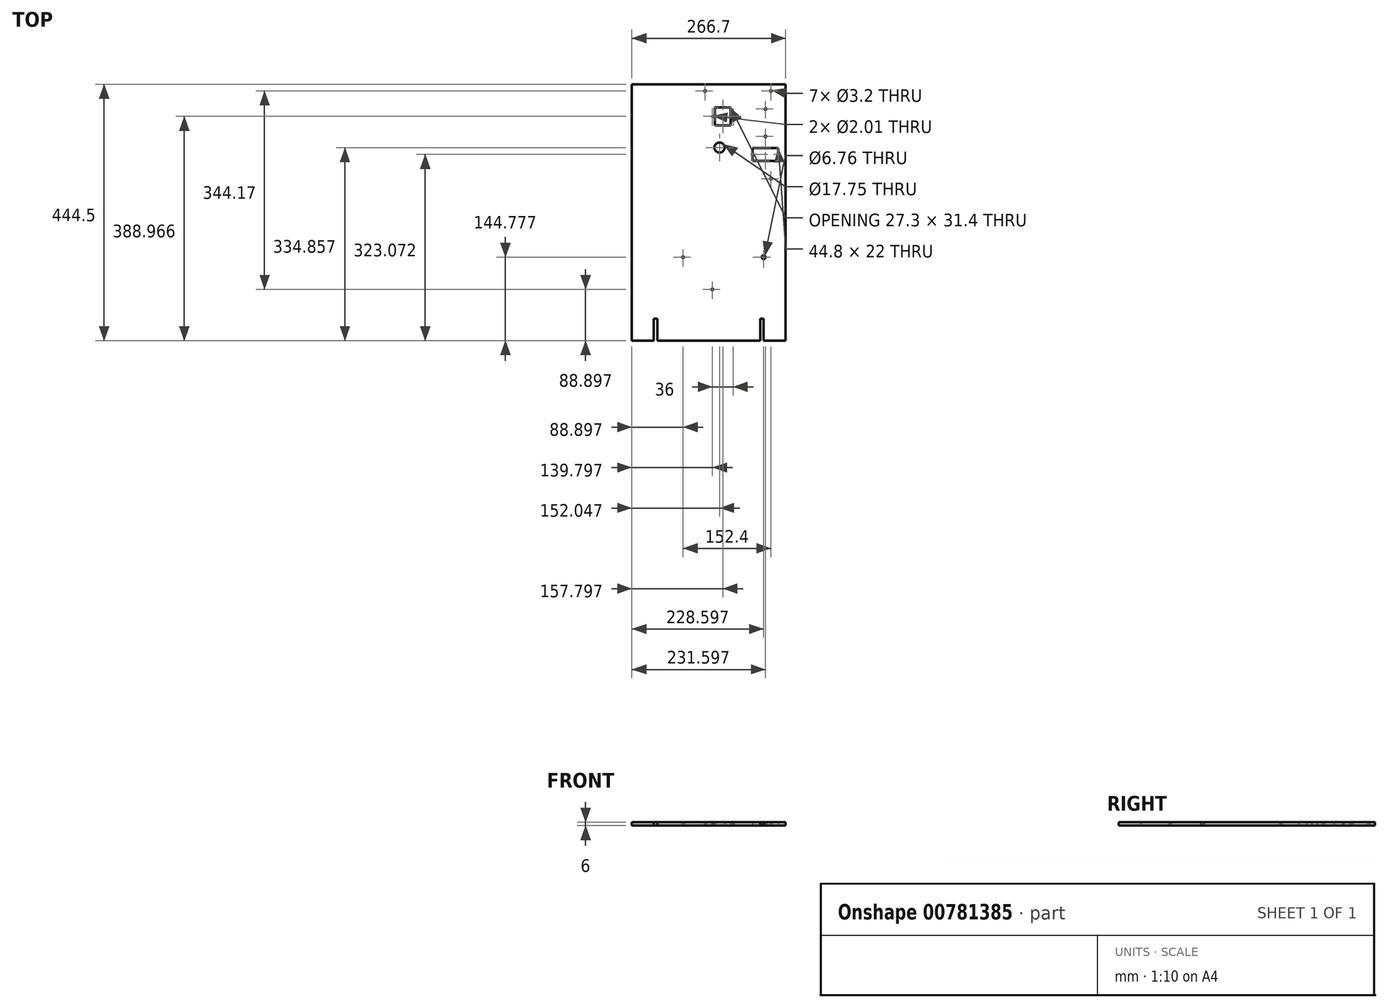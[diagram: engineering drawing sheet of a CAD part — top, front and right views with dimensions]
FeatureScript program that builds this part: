
annotation { "Feature Type Name" : "Feature", "Feature Type Description" : "" }
export const myFeature = defineFeature(function(context is Context, id is Id, definition is map)
    precondition{}
    {
        {
            var Q0;
            Q0=qCreatedBy(makeId("Top.planeOp"),FACE);
            var sketch = newSketch(context, id + "F0", { "sketchPlane" : qUnion([Q0])});
            skLineSegment(sketch, "E0.bottom", {"start": v(-111.5, 268) * mm, "end": v(155.2, 268) * mm});
            skLineSegment(sketch, "E0.top", {"start": v(-111.5, -176.5) * mm, "end": v(-73.4, -176.5) * mm});
            skLineSegment(sketch, "E0.left", {"start": v(-111.5, 268) * mm, "end": v(-111.5, -176.5) * mm});
            skLineSegment(sketch, "E0.right", {"start": v(155.2, 268) * mm, "end": v(155.2, -176.5) * mm});
            skCircle(sketch, "E1", {"center": v(117.1, -31.71) * mm, "radius": 3.38 * mm});
            skCircle(sketch, "E2", {"center": v(129.8, 104.18) * mm, "radius": 1.6 * mm});
            skCircle(sketch, "E3", {"center": v(129.8, 256.58) * mm, "radius": 1.6 * mm});
            skCircle(sketch, "E4", {"center": v(28.2, -87.6) * mm, "radius": 1.6 * mm});
            skCircle(sketch, "E5", {"center": v(-22.6, -31.71) * mm, "radius": 1.6 * mm});
            skCircle(sketch, "E6", {"center": v(15.5, 256.58) * mm, "radius": 1.6 * mm});
            skLineSegment(sketch, "E7.top", {"start": v(-73.4, -138.4) * mm, "end": v(-67.4, -138.4) * mm});
            skLineSegment(sketch, "E7.left", {"start": v(-73.4, -176.5) * mm, "end": v(-73.4, -138.4) * mm});
            skLineSegment(sketch, "E7.right", {"start": v(-67.4, -176.5) * mm, "end": v(-67.4, -138.4) * mm});
            skLineSegment(sketch, "E8.trimOffspring", {"start": v(-67.4, -176.5) * mm, "end": v(111.1, -176.5) * mm});
            skLineSegment(sketch, "E9.top", {"start": v(111.1, -138.4) * mm, "end": v(117.1, -138.4) * mm});
            skLineSegment(sketch, "E9.left", {"start": v(111.1, -176.5) * mm, "end": v(111.1, -138.4) * mm});
            skLineSegment(sketch, "E9.right", {"start": v(117.1, -176.5) * mm, "end": v(117.1, -138.4) * mm});
            skLineSegment(sketch, "E10.trimOffspring", {"start": v(117.1, -176.5) * mm, "end": v(155.2, -176.5) * mm});
            skLineSegment(sketch, "E11", {"start": v(155.2, 237.53) * mm, "end": v(-9.9, 237.53) * mm, "construction": true});
            skLineSegment(sketch, "E12", {"start": v(-9.9, 237.53) * mm, "end": v(-9.9, 123.23) * mm, "construction": true});
            skLineSegment(sketch, "E13", {"start": v(-9.9, 123.23) * mm, "end": v(155.2, 123.23) * mm, "construction": true});
            skLineSegment(sketch, "E14.bottom", {"start": v(98.05, 229.97) * mm, "end": v(142.5, 229.97) * mm, "construction": true});
            skLineSegment(sketch, "E14.top", {"start": v(98.05, 172.82) * mm, "end": v(142.5, 172.82) * mm, "construction": true});
            skLineSegment(sketch, "E14.left", {"start": v(98.05, 229.97) * mm, "end": v(98.05, 172.82) * mm, "construction": true});
            skLineSegment(sketch, "E14.right", {"start": v(142.5, 229.97) * mm, "end": v(142.5, 172.82) * mm, "construction": true});
            skPoint(sketch, "E15", {"position": v(120.27, 229.97) * mm});
            skCircle(sketch, "E16", {"center": v(120.27, 177.74) * mm, "radius": 1.6 * mm});
            skLineSegment(sketch, "E17.bottom", {"start": v(97.7, 157.58) * mm, "end": v(142.5, 157.58) * mm});
            skLineSegment(sketch, "E17.top", {"start": v(97.7, 135.58) * mm, "end": v(142.5, 135.58) * mm});
            skLineSegment(sketch, "E17.left", {"start": v(97.7, 157.58) * mm, "end": v(97.7, 135.58) * mm});
            skLineSegment(sketch, "E17.right", {"start": v(142.5, 157.58) * mm, "end": v(142.5, 135.58) * mm});
            skLineSegment(sketch, "E18.bottom", {"start": v(33.65, 228.18) * mm, "end": v(58.95, 228.18) * mm});
            skLineSegment(sketch, "E18.top", {"start": v(33.65, 196.78) * mm, "end": v(58.95, 196.78) * mm});
            skLineSegment(sketch, "E18.left", {"start": v(32.65, 227.18) * mm, "end": v(32.65, 197.78) * mm});
            skLineSegment(sketch, "E18.right", {"start": v(59.95, 227.18) * mm, "end": v(59.95, 197.78) * mm});
            skLineSegment(sketch, "E19", {"start": v(28.3, 212.48) * mm, "end": v(64.3, 212.48) * mm, "construction": true});
            skPoint(sketch, "E19.startSnap0", {"position": v(32.65, 212.48) * mm});
            skCircle(sketch, "E20", {"center": v(64.3, 212.48) * mm, "radius": 1 * mm});
            skCircle(sketch, "E21", {"center": v(28.3, 212.48) * mm, "radius": 1 * mm});
            skPoint(sketch, "E22", {"position": v(59.95, 212.48) * mm});
            skPoint(sketch, "E23", {"position": v(46.3, 212.48) * mm});
            skPoint(sketch, "E24", {"position": v(46.3, 228.18) * mm});
            skPoint(sketch, "E25.visualSharp", {"position": v(32.65, 228.18) * mm});
            skArc(sketch, "E25.filletArc", {"start": v(33.65, 228.18) * mm, "mid": v(32.94, 227.88) * mm, "end": v(32.65, 227.18) * mm});
            skPoint(sketch, "E26.visualSharp", {"position": v(59.95, 228.18) * mm});
            skArc(sketch, "E26.filletArc", {"start": v(59.95, 227.18) * mm, "mid": v(59.65, 227.88) * mm, "end": v(58.95, 228.18) * mm});
            skPoint(sketch, "E27.visualSharp", {"position": v(59.95, 196.78) * mm});
            skArc(sketch, "E27.filletArc", {"start": v(58.95, 196.78) * mm, "mid": v(59.65, 197.07) * mm, "end": v(59.95, 197.78) * mm});
            skPoint(sketch, "E28.visualSharp", {"position": v(32.65, 196.78) * mm});
            skArc(sketch, "E28.filletArc", {"start": v(32.65, 197.78) * mm, "mid": v(32.94, 197.07) * mm, "end": v(33.65, 196.78) * mm});
            skCircle(sketch, "E29", {"center": v(40.55, 158.37) * mm, "radius": 8.87 * mm});
            skCircle(sketch, "E30", {"center": v(120.27, 225.23) * mm, "radius": 1.6 * mm});
            skSolve(sketch);
        }
        {
            var Q0;
            Q0 = qSketchRegion(id + "F0", true);
            extrude(context, id + "F1", {"entities" : qUnion([Q0]), "depth" : 6 * mm, "offsetDistance" : 25.4 * mm});
        }
    });
